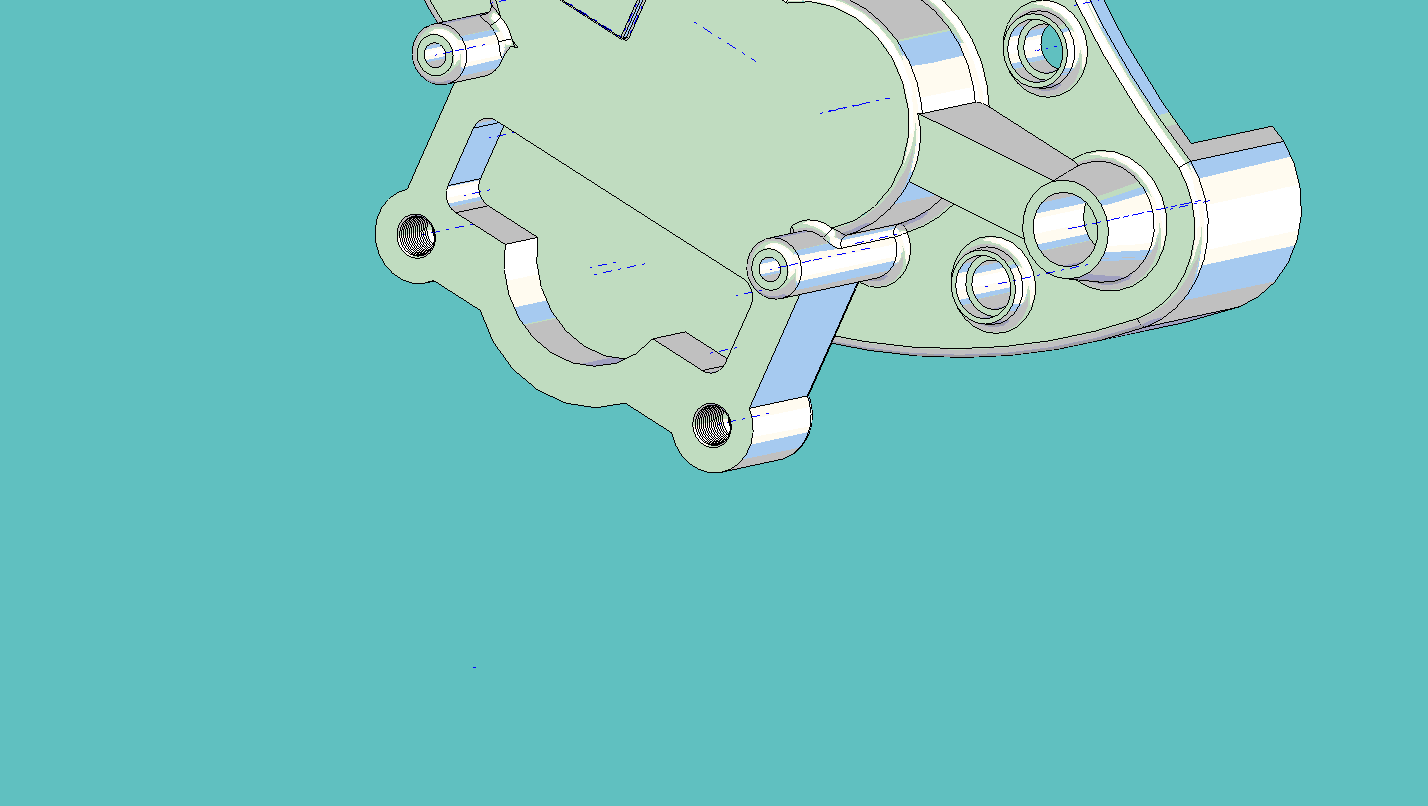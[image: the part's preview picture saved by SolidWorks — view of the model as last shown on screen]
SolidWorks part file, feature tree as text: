
SOLIDWORKS PART (.sldprt)
format: sldprt  version: not decoded by parser v0  size: 2,243,072 bytes
history: native  units: mm
features: sketch x29, cut_extrude x14, fillet x9, extrude x7, plane x5, mirror x4, sweep x2, pattern_linear x2, material x1, chamfer x1, delete_body x1 (+13 scaffold rows collapsed)
feature tree (88):
  scaffold x13  (default folders/planes/origin — collapsed)
  material  "Material <not specified>"
  sketch  "Sketch1"  dims[D1=63.5mm]
  extrude  "Extrude1"  Depth=31.75mm
  sketch  "Sketch5"  dims[D1=~43.962388mm]
  extrude  "Extrude2"  Depth=50.8mm
  sketch  "Sketch3"  dims[D1=50.0mm]
  cut_extrude  "Cut-Extrude1"  Depth=25.4mm
  sketch  "Sketch7"  dims[c1.D1=12.7mm c1.D2=12.7mm c2.D1=~13.906952mm c2.D2=25.0mm c2.D3=25.0mm c3.D1=~12.799272mm c3.D3=152.4mm]
  fillet  "Fillet1"  Radius=2.54mm
  fillet  "Fillet2"  Radius=2.54mm
  fillet  "Fillet3"  Radius=2.54mm
  sketch  "Sketch10"
  cut_extrude  "Cut-Extrude3"  [1 undecoded]
  plane  "Plane1"  Offset=10.16mm
  plane  "Plane2"  Offset=8.636mm
  sketch  "Sketch13"  dims[D1=273.05mm D2=137.16mm]
  cut_extrude  "Cut-Extrude4"  [1 undecoded]
  sketch  "Sketch14"
  cut_extrude  "Cut-Extrude5"  [1 undecoded]
  sketch  "Sketch15"
  extrude  "Extrude3"  Depth=53.18mm
  fillet  "Fillet4"  Radius=2.54mm
  sketch  "Sketch16"  dims[D1=~1.636236mm]
  cut_extrude  "Cut-Extrude6"  Depth=27.94mm
  fillet  "Fillet5"  Radius=2.54mm
  sketch  "Sketch17"
  extrude  "Extrude4"  Depth=2.54mm
  fillet  "Fillet6"  Radius=0.508mm
  chamfer  "Chamfer1"  Distance=1.27mm Angle=45deg
  sketch  "Sketch20"  dims[c1.D1=31.75mm c1.D2=25.4mm c2.D1=~20.003376mm]
  extrude  "Extrude5"  Depth=20.32mm
  cut_extrude  "Cut-Extrude8"  [1 undecoded]
  sketch  "Sketch21"  dims[D1=~4.108238mm]
  cut_extrude  "Cut-Extrude10"  Depth=25.4mm
  fillet  "Fillet7"  Radius=2.54mm
  sketch  "Sketch22"  dims[D1=10.16mm]
  cut_extrude  "Cut-Extrude11"  [1 undecoded]
  sketch  "Sketch24"
  cut_extrude  "Cut-Extrude12"  Depth=22.86mm
  sketch  "Sketch25"  dims[D1=20.574mm]
  extrude  "Extrude6"  Depth=5.08mm
  fillet  "Fillet8"  Radius=2.54mm
  sketch  "Sketch27"  dims[D1=~16.253517mm]
  cut_extrude  "Cut-Extrude15"  Depth=5.08mm
  mirror  "Mirror1"
  sketch  "Sketch29"  dims[D1=7.62mm]
  extrude  "Extrude7"  [1 undecoded]
  sketch  "Sketch30"
  sketch  "Sketch31"  dims[D1=5.08mm]
  cut_extrude  "Cut-Extrude18"  Depth=16.392582mm
  sketch  "Sketch32"  dims[D1=8.89mm]
  cut_extrude  "Cut-Extrude19"  Depth=16.392582mm
  cut_extrude  "Cut-Extrude20"  Depth=43.688mm
  sketch  "Sketch33"
  cut_extrude  "Cut-Extrude21"  Depth=59.69mm
  fillet  "Fillet11"  Radius=2.54mm
  plane  "Plane3"  Offset=94.488mm
  sketch  "Sketch34"  dims[D1=17.62mm]
  sketch  "Sketch36"
  mirror  "Rib3"
  sketch  "Sketch38"
  mirror  "Rib4"
  sketch  "Sketch40"
  mirror  "Rib5"
  delete_body  "Body-Delete1"
  plane  "Plane4"  Offset=50.8mm
  sketch  "Sketch42"
  sketch  "Sketch43"
  sweep  "Cut-Sweep1"
  pattern_linear  "LPattern1"  Count1=16 Count2=1 Spacing1=0.978mm Spacing2=50mm
  plane  "Plane5"  Offset=46.482mm
  sketch  "Sketch46"
  sketch  "Sketch47"
  sweep  "Cut-Sweep2"
  pattern_linear  "LPattern2"  Count1=16 Count2=1 Spacing1=0.978mm Spacing2=50mm
decode coverage: 42 of 69 modeling features carry decoded parameters
note: ~ marks probable driven/reference dimensions
note: 6 parameter values undecoded
summary: no parameter record found for 6 features
note: suppression state not decoded; provenance and decode notes live in map.json
